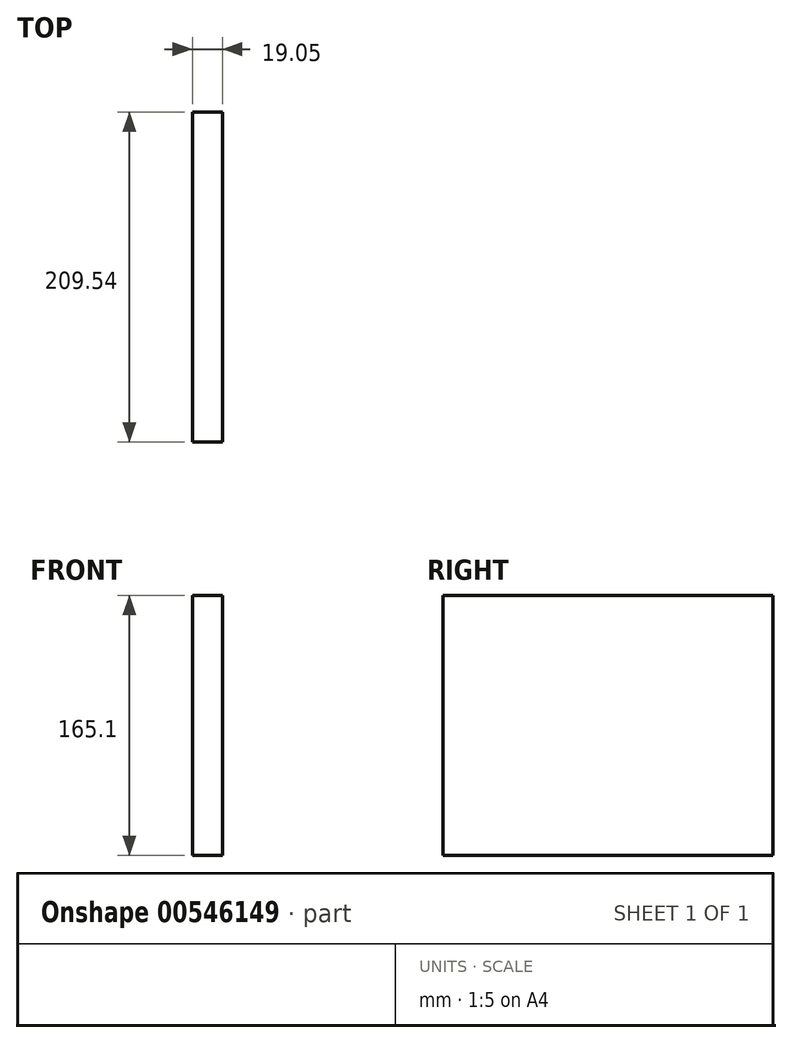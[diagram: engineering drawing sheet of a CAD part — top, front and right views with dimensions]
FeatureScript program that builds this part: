
annotation { "Feature Type Name" : "Feature", "Feature Type Description" : "" }
export const myFeature = defineFeature(function(context is Context, id is Id, definition is map)
    precondition{}
    {
        {
            var Q0;
            Q0=qCreatedBy(makeId("Right.planeOp"),FACE);
            var sketch = newSketch(context, id + "F0", { "sketchPlane" : qUnion([Q0])});
            skLineSegment(sketch, "E0.bottom", {"start": v(-104.78, 82.55) * mm, "end": v(104.78, 82.55) * mm});
            skLineSegment(sketch, "E0.top", {"start": v(-104.78, -82.55) * mm, "end": v(104.78, -82.55) * mm});
            skLineSegment(sketch, "E0.left", {"start": v(-104.78, 82.55) * mm, "end": v(-104.78, -82.55) * mm});
            skLineSegment(sketch, "E0.right", {"start": v(104.78, 82.55) * mm, "end": v(104.78, -82.55) * mm});
            skPoint(sketch, "E0.middle", {"position": v(0, 0) * mm});
            skSolve(sketch);
        }
        {
            var Q0;
            Q0=makeQuery(id+"F0.imprint","IMPRINT",FACE,{"disambiguationData":[TD([[makeQuery(id+"F0.imprint","IMPRINT",EDGE,{"derivedFrom":sQuery(id+"F0.wireOp",EDGE,"E0.bottom")}),-1.0]])]});
            extrude(context, id + "F1", {"entities" : qUnion([Q0]), "depth" : 19.05 * mm, "offsetDistance" : 25.4 * mm});
        }
    });
